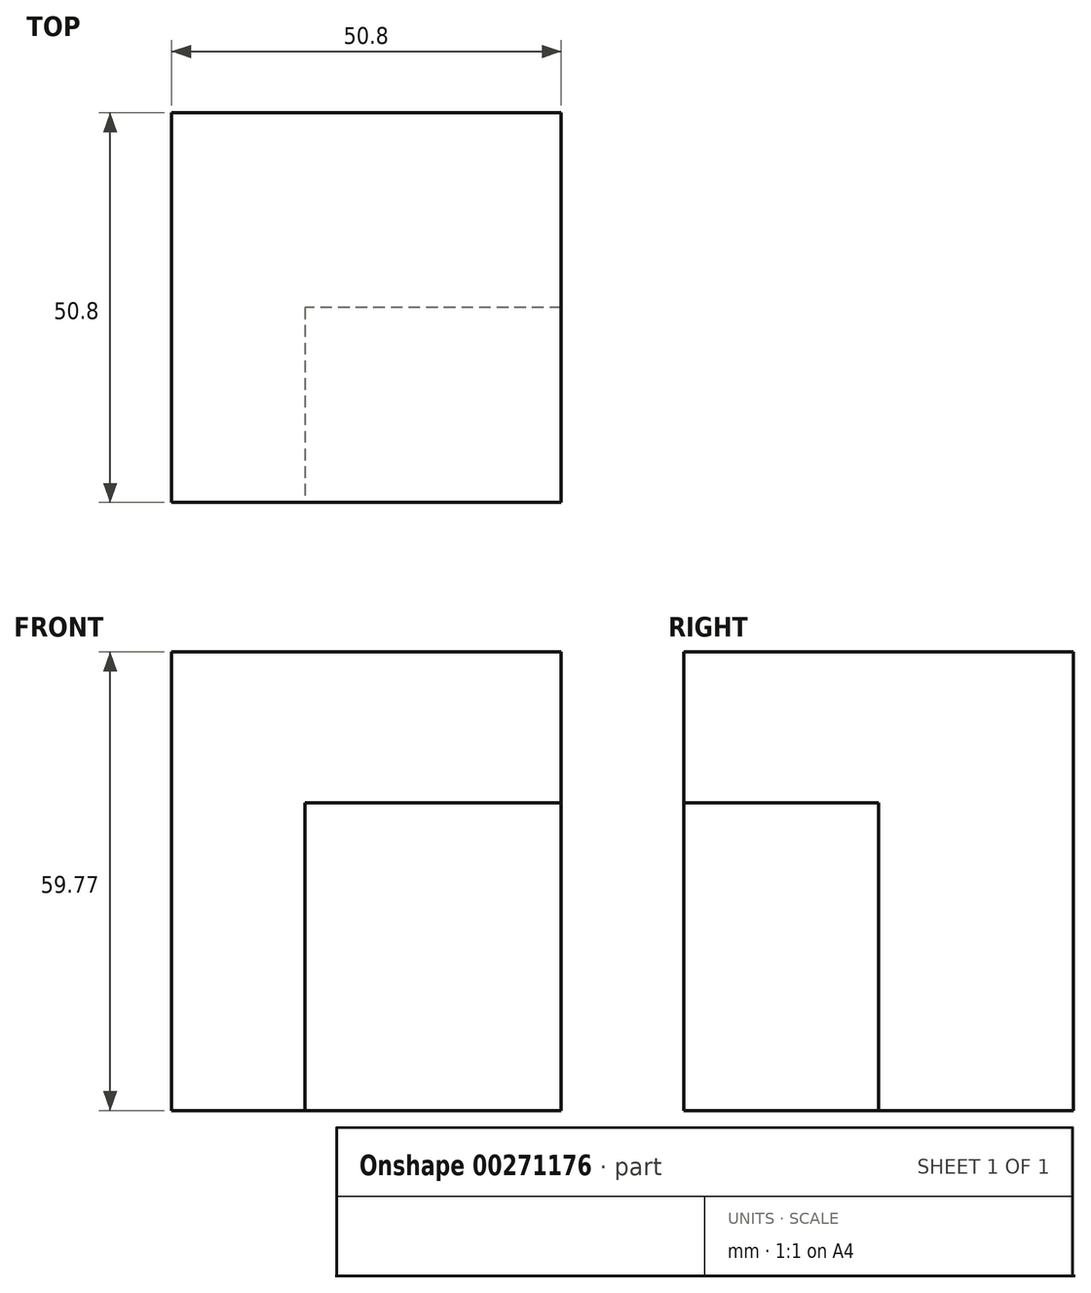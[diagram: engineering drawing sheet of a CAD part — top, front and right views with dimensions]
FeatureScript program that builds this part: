
annotation { "Feature Type Name" : "Feature", "Feature Type Description" : "" }
export const myFeature = defineFeature(function(context is Context, id is Id, definition is map)
    precondition{}
    {
        {
            var Q0;
            Q0=qCreatedBy(makeId("Front.planeOp"),FACE);
            var sketch = newSketch(context, id + "F0", { "sketchPlane" : qUnion([Q0])});
            skLineSegment(sketch, "E0.bottom", {"start": v(0, 0) * mm, "end": v(-50.8, 0) * mm});
            skLineSegment(sketch, "E0.top", {"start": v(0, 59.77) * mm, "end": v(-50.8, 59.77) * mm});
            skLineSegment(sketch, "E0.left", {"start": v(0, 0) * mm, "end": v(0, 59.77) * mm});
            skLineSegment(sketch, "E0.right", {"start": v(-50.8, 0) * mm, "end": v(-50.8, 59.77) * mm});
            skSolve(sketch);
        }
        {
            var Q0;
            Q0 = qSketchRegion(id + "F0", true);
            extrude(context, id + "F1", {"entities" : qUnion([Q0]), "depth" : 50.8 * mm});
        }
        {
            var Q0;
            Q0=makeQuery(id+"F1.opExtrude","CAP_FACE",FACE,{"disambiguationData":[OSD([sQuery(id+"F0.wireOp",EDGE,"E0.bottom"),sQuery(id+"F0.wireOp",EDGE,"E0.top"),sQuery(id+"F0.wireOp",EDGE,"E0.left"),sQuery(id+"F0.wireOp",EDGE,"E0.right")])],"isStart":false});
            var sketch = newSketch(context, id + "F2", { "sketchPlane" : qUnion([Q0])});
            skLineSegment(sketch, "E1.bottom", {"start": v(0, 0) * mm, "end": v(-33.8, 0) * mm});
            skLineSegment(sketch, "E1.top", {"start": v(0, 40.1) * mm, "end": v(-33.8, 40.1) * mm});
            skLineSegment(sketch, "E1.left", {"start": v(0, 0) * mm, "end": v(0, 40.1) * mm});
            skLineSegment(sketch, "E1.right", {"start": v(-33.8, 0) * mm, "end": v(-33.8, 40.1) * mm});
            skSolve(sketch);
        }
        {
            var Q0;
            Q0=makeQuery(id+"F2.imprint","IMPRINT",FACE,{"disambiguationData":[TD([[makeQuery(id+"F2.imprint","IMPRINT",EDGE,{"derivedFrom":sQuery(id+"F2.wireOp",EDGE,"E1.bottom")}),-1.0]])]});
            var sketch = newSketch(context, id + "F3", { "sketchPlane" : qUnion([Q0])});
            skLineSegment(sketch, "E2.bottom", {"start": v(0, 0) * mm, "end": v(-33.42, 0) * mm});
            skLineSegment(sketch, "E2.top", {"start": v(0, 40.1) * mm, "end": v(-33.42, 40.1) * mm});
            skLineSegment(sketch, "E2.left", {"start": v(0, 0) * mm, "end": v(0, 40.1) * mm});
            skLineSegment(sketch, "E2.right", {"start": v(-33.42, 0) * mm, "end": v(-33.42, 40.1) * mm});
            skSolve(sketch);
        }
        {
            var Q0;
            Q0 = qSketchRegion(id + "F3", true);
            extrude(context, id + "F4", {"entities" : qUnion([Q0]), "operationType" : NewBodyOperationType.REMOVE, "oppositeDirection" : true, "depth" : 25.4 * mm});
        }
    });
